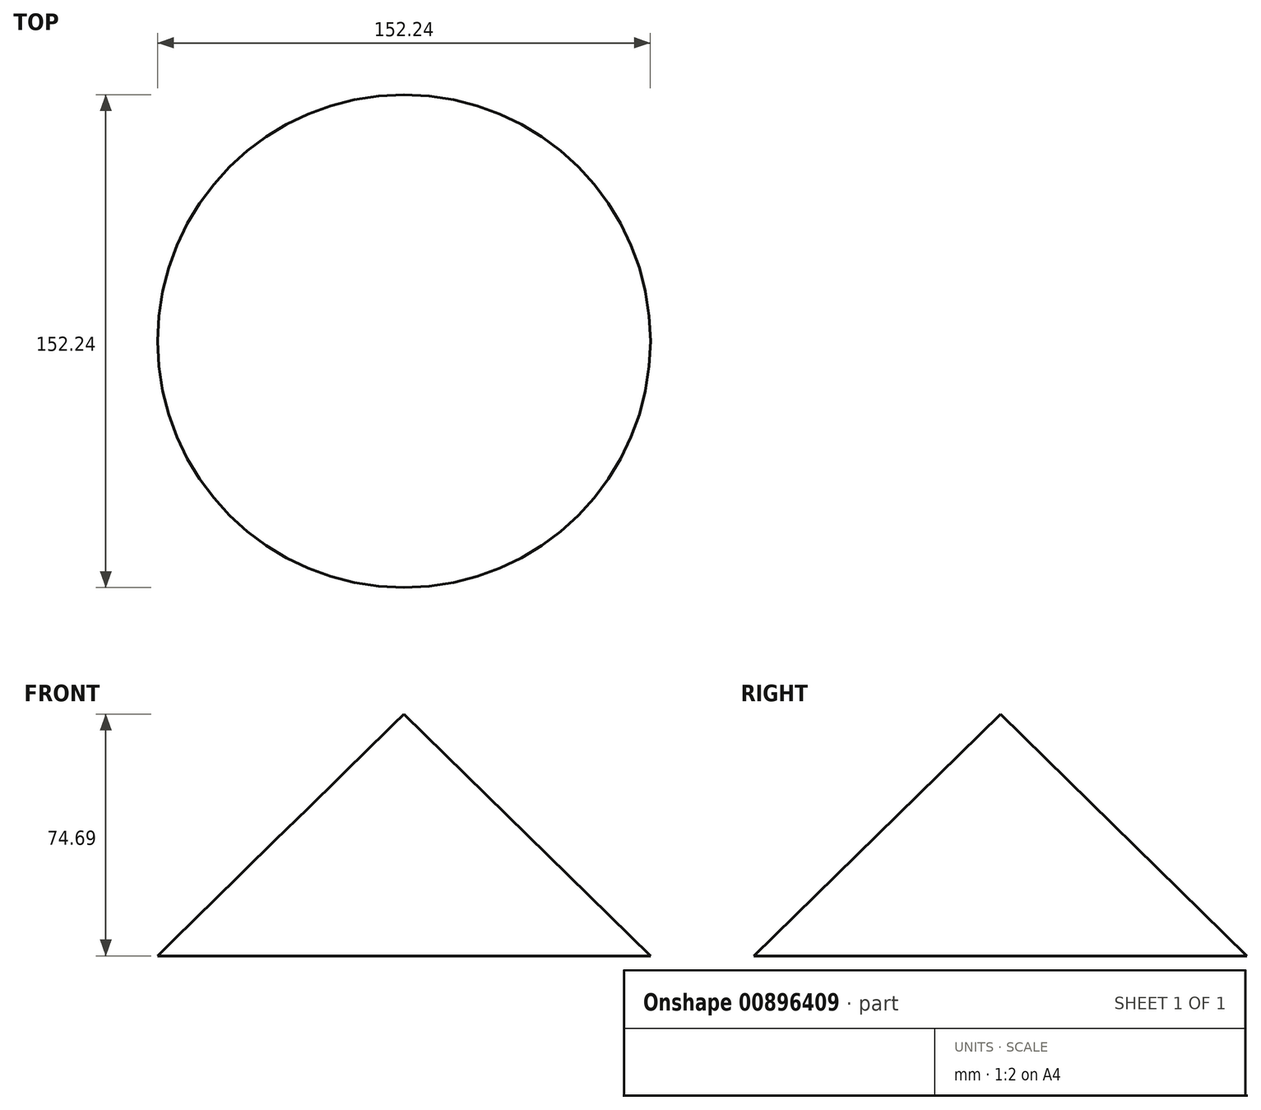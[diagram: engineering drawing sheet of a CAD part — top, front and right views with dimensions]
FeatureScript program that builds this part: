
annotation { "Feature Type Name" : "Feature", "Feature Type Description" : "" }
export const myFeature = defineFeature(function(context is Context, id is Id, definition is map)
    precondition{}
    {
        {
            var Q0;
            Q0=qCreatedBy(makeId("Front.planeOp"),FACE);
            var sketch = newSketch(context, id + "F0", { "sketchPlane" : qUnion([Q0])});
            skLineSegment(sketch, "E0", {"start": v(0, -2.45) * mm, "end": v(0, 74.69) * mm});
            skLineSegment(sketch, "E1", {"start": v(0, 74.69) * mm, "end": v(-76.12, 0) * mm});
            skLineSegment(sketch, "E2", {"start": v(-76.12, 0) * mm, "end": v(0, 0) * mm});
            skSolve(sketch);
        }
        {
            var Q0;
            Q0 = qSketchRegion(id + "F0", true);
            var Q1;
            Q1=sQuery(id+"F0.wireOp",EDGE,"E0");
            revolve(context, id + "F1", {"surfaceOperationType" : NewSurfaceOperationType.NEW, "entities" : qUnion([Q0]), "axis" : qUnion([Q1]), "revolveType" : RevolveType.FULL});
        }
    });
